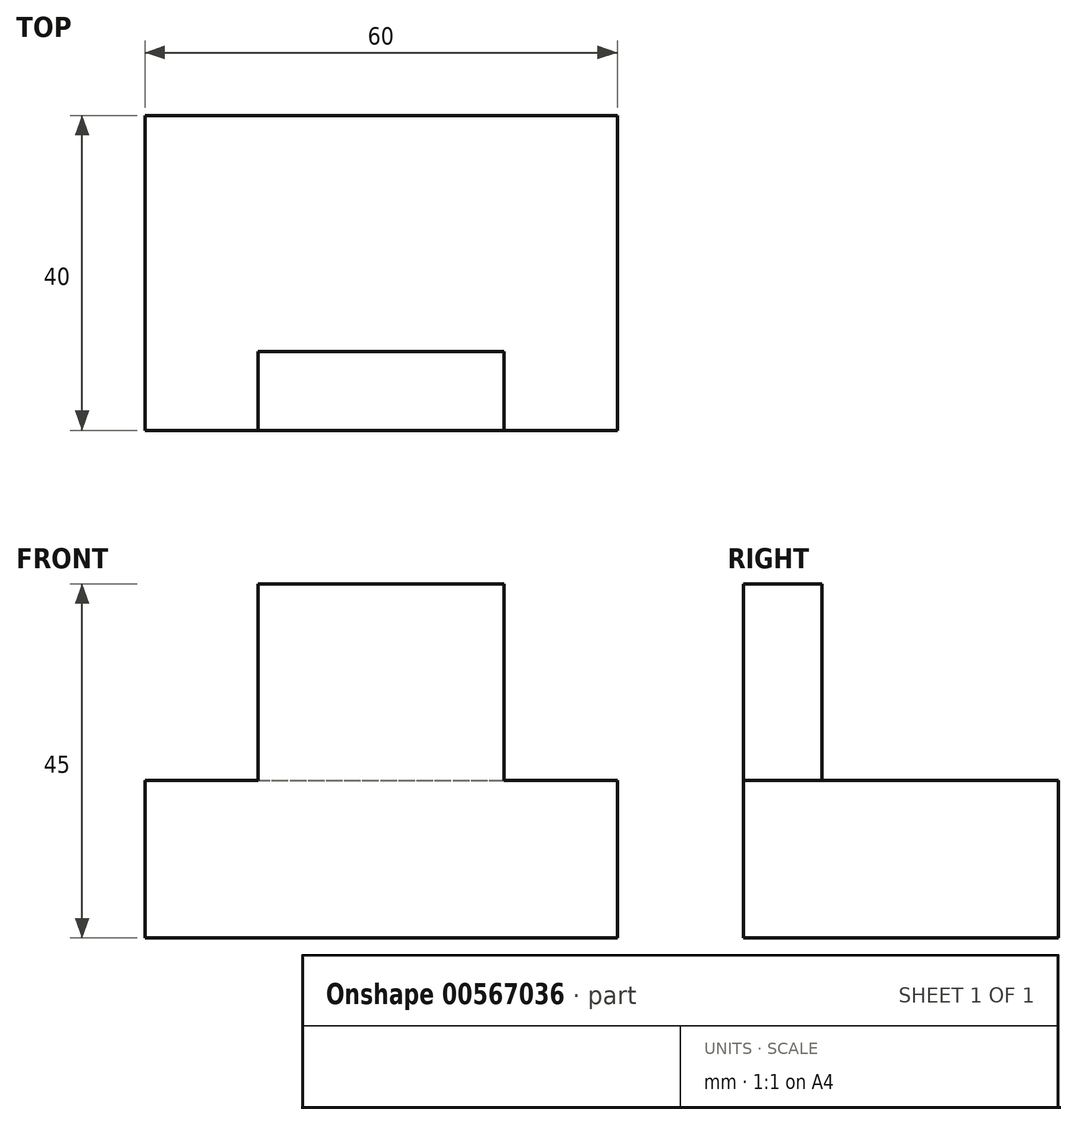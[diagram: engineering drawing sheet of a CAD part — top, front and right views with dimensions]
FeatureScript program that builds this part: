
annotation { "Feature Type Name" : "Feature", "Feature Type Description" : "" }
export const myFeature = defineFeature(function(context is Context, id is Id, definition is map)
    precondition{}
    {
        {
            var Q0;
            Q0=qCreatedBy(makeId("Top.planeOp"),FACE);
            var sketch = newSketch(context, id + "F0", { "sketchPlane" : qUnion([Q0])});
            skLineSegment(sketch, "E0.bottom", {"start": v(-30, 40) * mm, "end": v(30, 40) * mm});
            skLineSegment(sketch, "E0.top", {"start": v(-30, 0) * mm, "end": v(30, 0) * mm});
            skLineSegment(sketch, "E0.left", {"start": v(-30, 40) * mm, "end": v(-30, 0) * mm});
            skLineSegment(sketch, "E0.right", {"start": v(30, 40) * mm, "end": v(30, 0) * mm});
            skSolve(sketch);
        }
        {
            var Q0;
            Q0=makeQuery(id+"F0.imprint","IMPRINT",FACE,{"disambiguationData":[TD([[makeQuery(id+"F0.imprint","IMPRINT",EDGE,{"derivedFrom":sQuery(id+"F0.wireOp",EDGE,"E0.bottom")}),-1.0]])]});
            extrude(context, id + "F1", {"entities" : qUnion([Q0]), "depth" : 20 * mm, "offsetDistance" : 25 * mm});
        }
        {
            var Q0;
            Q0=makeQuery(id+"F1.opExtrude","CAP_FACE",FACE,{"disambiguationData":[OSD([sQuery(id+"F0.wireOp",EDGE,"E0.bottom"),sQuery(id+"F0.wireOp",EDGE,"E0.top"),sQuery(id+"F0.wireOp",EDGE,"E0.left"),sQuery(id+"F0.wireOp",EDGE,"E0.right")])],"isStart":false});
            var sketch = newSketch(context, id + "F2", { "sketchPlane" : qUnion([Q0])});
            skLineSegment(sketch, "E1.bottom", {"start": v(-15.6, 0) * mm, "end": v(15.6, 0) * mm});
            skLineSegment(sketch, "E1.top", {"start": v(-15.6, 10) * mm, "end": v(15.6, 10) * mm});
            skLineSegment(sketch, "E1.left", {"start": v(-15.6, 0) * mm, "end": v(-15.6, 10) * mm});
            skLineSegment(sketch, "E1.right", {"start": v(15.6, 0) * mm, "end": v(15.6, 10) * mm});
            skLineSegment(sketch, "E2", {"start": v(0, 0) * mm, "end": v(0, -20) * mm, "construction": true});
            skSolve(sketch);
        }
        {
            var Q0;
            Q0=makeQuery(id+"F2.imprint","IMPRINT",FACE,{"disambiguationData":[TD([[makeQuery(id+"F2.imprint","IMPRINT",EDGE,{"derivedFrom":sQuery(id+"F2.wireOp",EDGE,"E1.bottom")}),1.0]])]});
            extrude(context, id + "F3", {"entities" : qUnion([Q0]), "operationType" : NewBodyOperationType.ADD, "depth" : 25 * mm, "offsetDistance" : 25 * mm});
        }
    });
